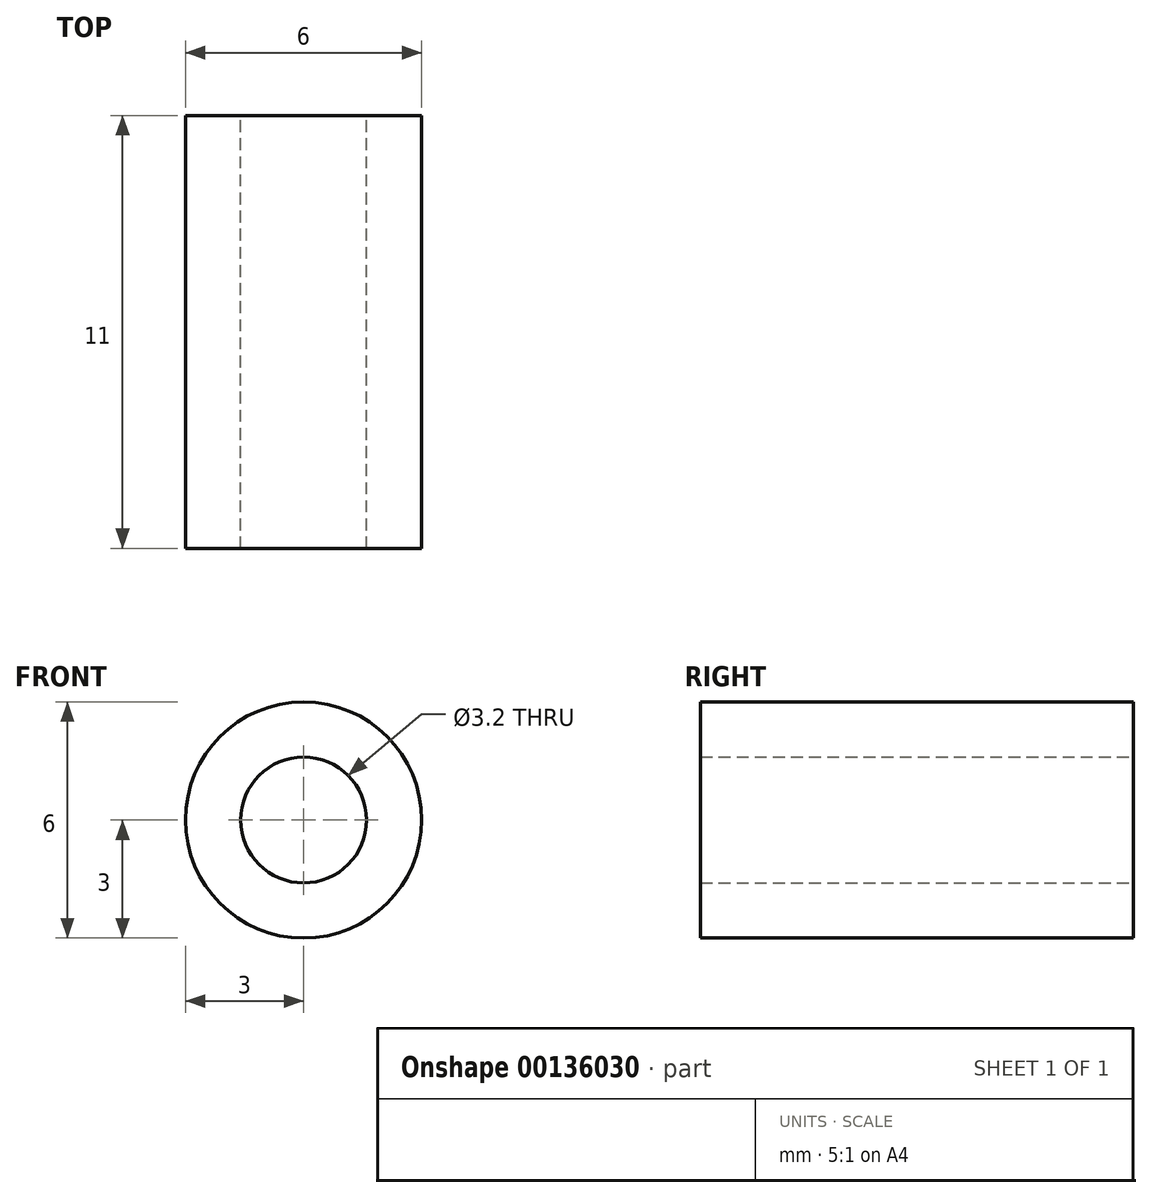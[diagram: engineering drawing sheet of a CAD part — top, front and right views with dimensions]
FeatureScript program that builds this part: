
annotation { "Feature Type Name" : "Feature", "Feature Type Description" : "" }
export const myFeature = defineFeature(function(context is Context, id is Id, definition is map)
    precondition{}
    {
        {
            var Q0;
            Q0=qCreatedBy(makeId("Front.planeOp"),FACE);
            var sketch = newSketch(context, id + "F0", { "sketchPlane" : qUnion([Q0])});
            skCircle(sketch, "E0", {"center": v(0, 0) * mm, "radius": 1.6 * mm});
            skCircle(sketch, "E1", {"center": v(0, 0) * mm, "radius": 3 * mm});
            skSolve(sketch);
        }
        {
            var Q0;
            Q0=makeQuery(id+"F0.imprint","IMPRINT",FACE,{"disambiguationData":[TD([[makeQuery(id+"F0.imprint","IMPRINT",EDGE,{"derivedFrom":sQuery(id+"F0.wireOp",EDGE,"E0")}),-1.0]])]});
            extrude(context, id + "F1", {"entities" : qUnion([Q0]), "depth" : 11 * mm});
        }
    });
